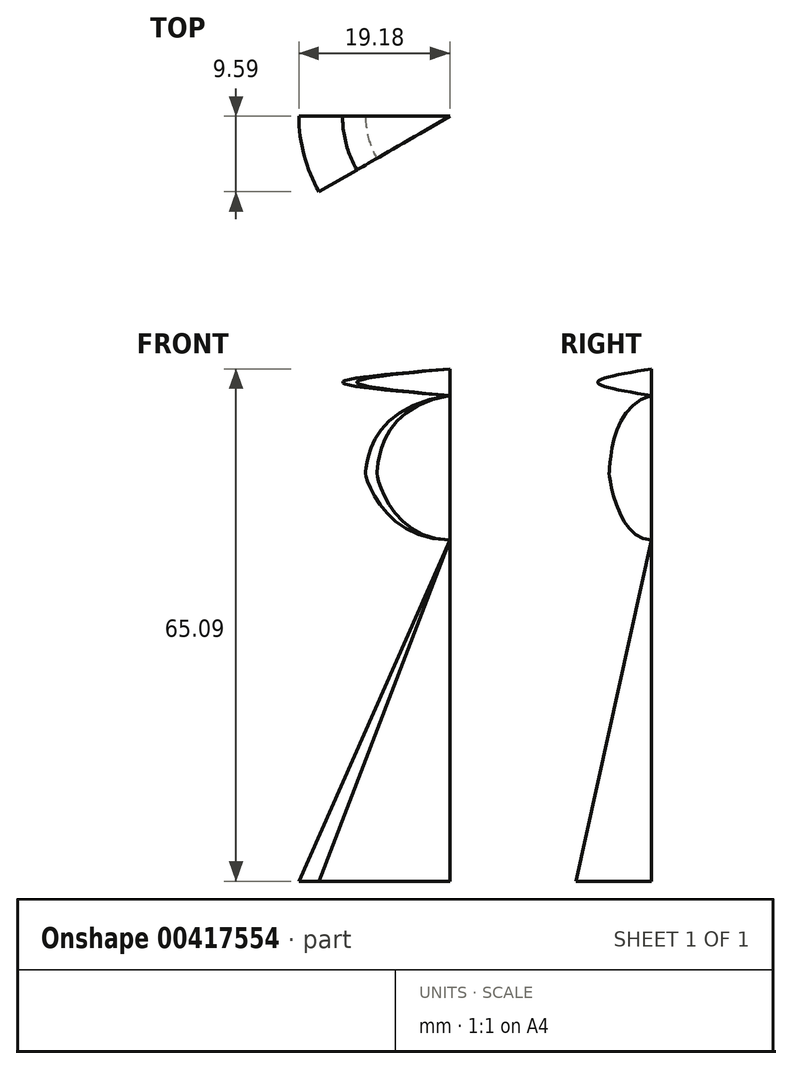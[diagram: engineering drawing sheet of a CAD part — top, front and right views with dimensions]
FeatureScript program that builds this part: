
annotation { "Feature Type Name" : "Feature", "Feature Type Description" : "" }
export const myFeature = defineFeature(function(context is Context, id is Id, definition is map)
    precondition{}
    {
        {
            var Q0;
            Q0=qCreatedBy(makeId("Front.planeOp"),FACE);
            var sketch = newSketch(context, id + "F0", { "sketchPlane" : qUnion([Q0])});
            skFitSpline(sketch, "E0", {"points": [v(0, 61.69) * mm, v(-10.65, 52.31) * mm, v(-10.65, 51.46) * mm, v(0, 43.36) * mm], "startDerivative": vector(-65.16, -8.5) * mm, "endDerivative": vector(52.52, 0) * mm});
            skLineSegment(sketch, "E1", {"start": v(0, 43.36) * mm, "end": v(-19.18, 0) * mm});
            skLineSegment(sketch, "E2", {"start": v(-19.18, 0) * mm, "end": v(0, 0) * mm});
            skLineSegment(sketch, "E3", {"start": v(0, 0) * mm, "end": v(0, 61.69) * mm});
            skFitSpline(sketch, "E4", {"points": [v(0, 61.69) * mm, v(-13.64, 63.4) * mm, v(0, 65.1) * mm], "startDerivative": vector(-40.91, 3.4) * mm, "endDerivative": vector(40.91, 3.4) * mm});
            skLineSegment(sketch, "E5", {"start": v(0, 61.69) * mm, "end": v(0, 65.1) * mm});
            skSolve(sketch);
        }
        {
            var Q0;
            Q0 = qSketchRegion(id + "F0", true);
            var Q1;
            Q1=sQuery(id+"F0.wireOp",EDGE,"E3");
            revolve(context, id + "F1", {"entities" : qUnion([Q0]), "axis" : qUnion([Q1]), "revolveType" : RevolveType.ONE_DIRECTION, "angle" : 30 * degree});
        }
    });
